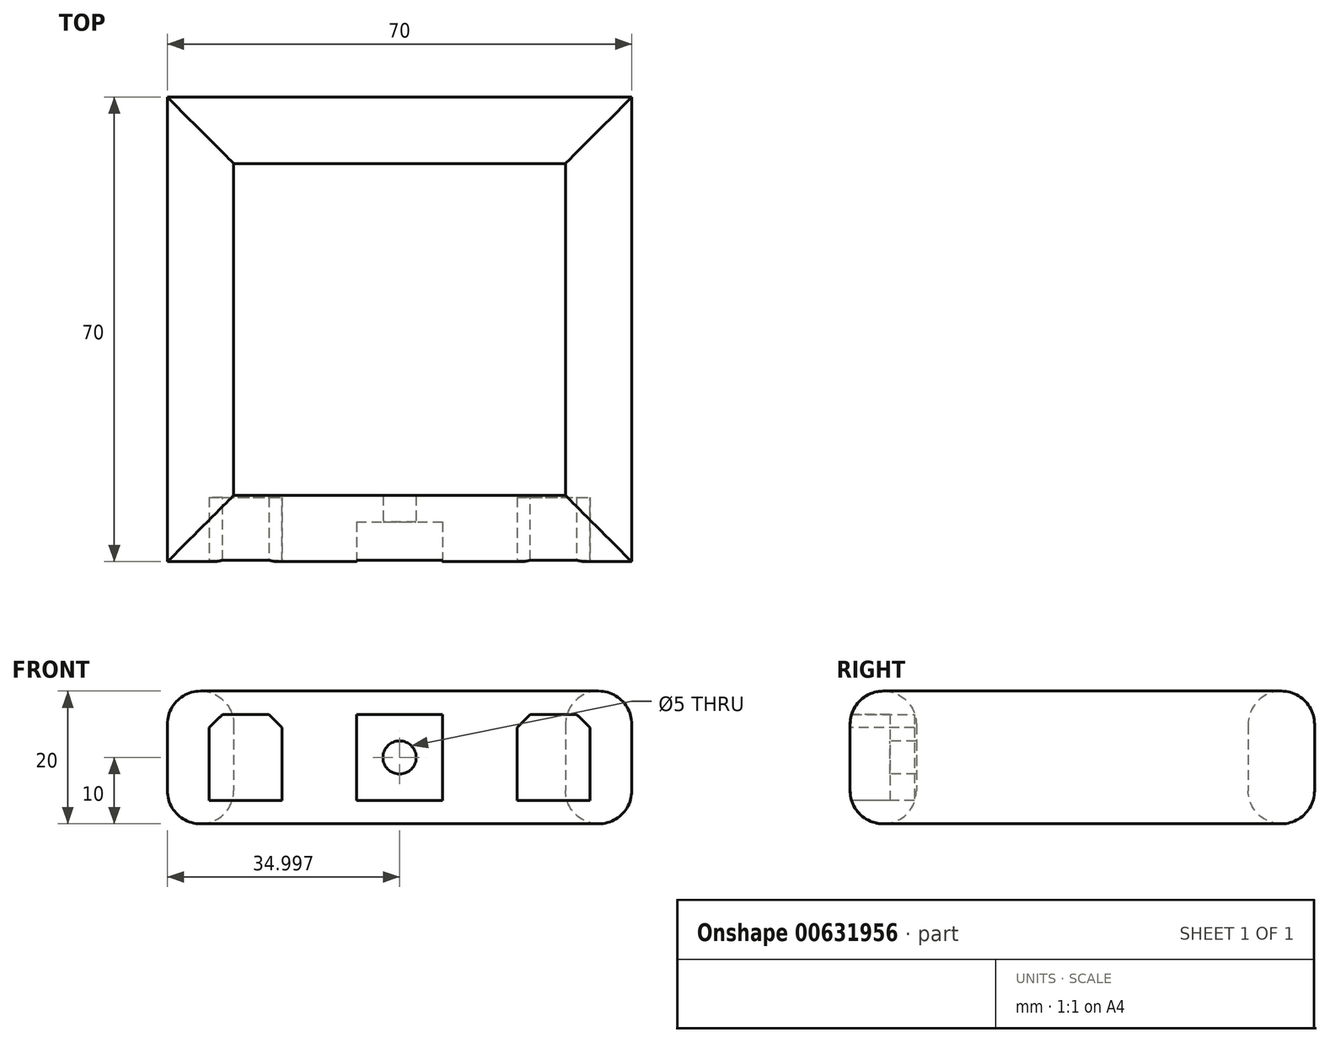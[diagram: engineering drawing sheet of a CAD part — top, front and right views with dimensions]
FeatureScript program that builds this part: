
annotation { "Feature Type Name" : "Feature", "Feature Type Description" : "" }
export const myFeature = defineFeature(function(context is Context, id is Id, definition is map)
    precondition{}
    {
        {
            var Q0;
            Q0=qCreatedBy(makeId("Top.planeOp"),FACE);
            var sketch = newSketch(context, id + "F0", { "sketchPlane" : qUnion([Q0])});
            skLineSegment(sketch, "E0.bottom", {"start": v(-28, 34.35) * mm, "end": v(42, 34.35) * mm});
            skLineSegment(sketch, "E0.top", {"start": v(-28, -35.65) * mm, "end": v(42, -35.65) * mm});
            skLineSegment(sketch, "E0.left", {"start": v(-28, 34.35) * mm, "end": v(-28, -35.65) * mm});
            skLineSegment(sketch, "E0.right", {"start": v(42, 34.35) * mm, "end": v(42, -35.65) * mm});
            skLineSegment(sketch, "E1.0", {"start": v(-18, 24.35) * mm, "end": v(-18, -25.65) * mm});
            skLineSegment(sketch, "E1.1", {"start": v(-18, 24.35) * mm, "end": v(32, 24.35) * mm});
            skLineSegment(sketch, "E1.2", {"start": v(32, 24.35) * mm, "end": v(32, -25.65) * mm});
            skLineSegment(sketch, "E1.3", {"start": v(-18, -25.65) * mm, "end": v(32, -25.65) * mm});
            skSolve(sketch);
        }
        {
            var Q0;
            Q0=makeQuery(id+"F0.imprint","IMPRINT",FACE,{"disambiguationData":[TD([[makeQuery(id+"F0.imprint","IMPRINT",EDGE,{"derivedFrom":sQuery(id+"F0.wireOp",EDGE,"E0.bottom")}),-1.0]])]});
            extrude(context, id + "F1", {"entities" : qUnion([Q0]), "depth" : 20 * mm, "offsetDistance" : 25 * mm});
        }
        {
            var Q0;
            Q0=makeQuery(id+"F1.opExtrude","SWEPT_FACE",FACE,{"disambiguationData":[OSD([sQuery(id+"F0.wireOp",EDGE,"E0.top")])]});
            var sketch = newSketch(context, id + "F2", { "sketchPlane" : qUnion([Q0])});
            skLineSegment(sketch, "E2.bottom", {"start": v(0.5, 16.5) * mm, "end": v(13.5, 16.5) * mm});
            skLineSegment(sketch, "E2.top", {"start": v(0.5, 3.5) * mm, "end": v(13.5, 3.5) * mm});
            skLineSegment(sketch, "E2.left", {"start": v(0.5, 16.5) * mm, "end": v(0.5, 3.5) * mm});
            skLineSegment(sketch, "E2.right", {"start": v(13.5, 16.5) * mm, "end": v(13.5, 3.5) * mm});
            skSolve(sketch);
        }
        {
            var Q0;
            Q0 = qSketchRegion(id + "F2", true);
            extrude(context, id + "F3", {"entities" : qUnion([Q0]), "operationType" : NewBodyOperationType.REMOVE, "oppositeDirection" : true, "depth" : 6 * mm, "offsetDistance" : 25 * mm});
        }
        {
            var Q0;
            Q0=makeQuery(id+"F7MwtvW5aFX19ho_1.boolean.opBoolean","MERGE",FACE,{"derivedFrom":[makeQuery(id+"FfgL2yHkp0veMAR_1.boolean.opBoolean","MERGE",FACE,{"derivedFrom":[makeQuery(id+"F1.opExtrude","CAP_FACE",FACE,{"disambiguationData":[OSD([sQuery(id+"F0.wireOp",EDGE,"E0.bottom"),sQuery(id+"F0.wireOp",EDGE,"E0.top"),sQuery(id+"F0.wireOp",EDGE,"E0.left"),sQuery(id+"F0.wireOp",EDGE,"E0.right"),sQuery(id+"F0.wireOp",EDGE,"E1.0"),sQuery(id+"F0.wireOp",EDGE,"E1.1"),sQuery(id+"F0.wireOp",EDGE,"E1.2"),sQuery(id+"F0.wireOp",EDGE,"E1.3")])],"isStart":false}),makeQuery(id+"FfgL2yHkp0veMAR_1.opExtrude","SWEPT_FACE",FACE,{"disambiguationData":[OSD([sQuery(id+"FrQLGLPTE21ChkL_1.wireOp",EDGE,"cfba748a-4d5a-4d7a-b181-aabee946887e.2")])]})]}),makeQuery(id+"F7MwtvW5aFX19ho_1.opExtrude","SWEPT_FACE",FACE,{"disambiguationData":[OSD([sQuery(id+"F9eCyIHyJgwxBDv_1.wireOp",EDGE,"g8lbYdjH-O4zc-bSOk-cj5n-4nt3Gmlz6ynf.top")])]})]});
            var Q1;
            Q1=makeQuery(id+"F7MwtvW5aFX19ho_1.boolean.opBoolean","MERGE",FACE,{"derivedFrom":[makeQuery(id+"FfgL2yHkp0veMAR_1.boolean.opBoolean","MERGE",FACE,{"derivedFrom":[makeQuery(id+"F1.opExtrude","CAP_FACE",FACE,{"disambiguationData":[OSD([sQuery(id+"F0.wireOp",EDGE,"E0.bottom"),sQuery(id+"F0.wireOp",EDGE,"E0.top"),sQuery(id+"F0.wireOp",EDGE,"E0.left"),sQuery(id+"F0.wireOp",EDGE,"E0.right"),sQuery(id+"F0.wireOp",EDGE,"E1.0"),sQuery(id+"F0.wireOp",EDGE,"E1.1"),sQuery(id+"F0.wireOp",EDGE,"E1.2"),sQuery(id+"F0.wireOp",EDGE,"E1.3")])],"isStart":true}),makeQuery(id+"FfgL2yHkp0veMAR_1.opExtrude","SWEPT_FACE",FACE,{"disambiguationData":[OSD([sQuery(id+"FrQLGLPTE21ChkL_1.wireOp",EDGE,"cfba748a-4d5a-4d7a-b181-aabee946887e.0")])]})]}),makeQuery(id+"F7MwtvW5aFX19ho_1.opExtrude","SWEPT_FACE",FACE,{"disambiguationData":[OSD([sQuery(id+"F9eCyIHyJgwxBDv_1.wireOp",EDGE,"g8lbYdjH-O4zc-bSOk-cj5n-4nt3Gmlz6ynf.bottom")])]})]});
            fillet(context, id + "F4", {"entities" : qUnion([Q0, Q1]), "radius" : 5 * mm, "tangentPropagation" : true, "allowEdgeOverflow" : false});
        }
        {
            var Q0;
            Q0=makeQuery(id+"F3.boolean.opBoolean","COPY",FACE,{"derivedFrom":makeQuery(id+"F3.opExtrude","CAP_FACE",FACE,{"disambiguationData":[OSD([sQuery(id+"F2.wireOp",EDGE,"E2.bottom"),sQuery(id+"F2.wireOp",EDGE,"E2.top"),sQuery(id+"F2.wireOp",EDGE,"E2.left"),sQuery(id+"F2.wireOp",EDGE,"E2.right")])],"isStart":false})});
            var sketch = newSketch(context, id + "F5", { "sketchPlane" : qUnion([Q0])});
            skCircle(sketch, "E3", {"center": v(7, 10) * mm, "radius": 2.5 * mm});
            skPoint(sketch, "E3.centerSnap0", {"position": v(7, 16.5) * mm});
            skPoint(sketch, "E3.centerSnap1", {"position": v(0.5, 10) * mm});
            skSolve(sketch);
        }
        {
            var Q0;
            Q0=makeQuery(id+"F5.imprint","IMPRINT",FACE,{"disambiguationData":[TD([[makeQuery(id+"F5.imprint","IMPRINT",EDGE,{"derivedFrom":sQuery(id+"F5.wireOp",EDGE,"E3")}),1.0]])]});
            extrude(context, id + "F6", {"entities" : qUnion([Q0]), "operationType" : NewBodyOperationType.REMOVE, "oppositeDirection" : true, "depth" : 25 * mm, "offsetDistance" : 25 * mm});
        }
        {
            var Q0;
            Q0=makeQuery(id+"F4.opFillet","SPLIT",FACE,{"disambiguationData":[OD(0.0)],"derivedFrom":makeQuery(id+"F1.opExtrude","SWEPT_FACE",FACE,{"disambiguationData":[OSD([sQuery(id+"F0.wireOp",EDGE,"E0.top")])]})});
            var sketch = newSketch(context, id + "F7", { "sketchPlane" : qUnion([Q0])});
            skLineSegment(sketch, "E4.bottom", {"start": v(-21.7, 16.5) * mm, "end": v(-10.7, 16.5) * mm});
            skLineSegment(sketch, "E4.top", {"start": v(-21.7, 3.5) * mm, "end": v(-10.7, 3.5) * mm});
            skLineSegment(sketch, "E4.left", {"start": v(-21.7, 16.5) * mm, "end": v(-21.7, 3.5) * mm});
            skLineSegment(sketch, "E4.right", {"start": v(-10.7, 16.5) * mm, "end": v(-10.7, 3.5) * mm});
            skLineSegment(sketch, "E5.1.0.0", {"start": v(24.7, 16.5) * mm, "end": v(24.7, 3.5) * mm});
            skLineSegment(sketch, "E5.1.0.1", {"start": v(24.7, 16.5) * mm, "end": v(35.7, 16.5) * mm});
            skLineSegment(sketch, "E5.1.0.2", {"start": v(35.7, 16.5) * mm, "end": v(35.7, 3.5) * mm});
            skLineSegment(sketch, "E5.1.0.3", {"start": v(24.7, 3.5) * mm, "end": v(35.7, 3.5) * mm});
            skLineSegment(sketch, "E5.direction1", {"start": v(-21.7, 3.5) * mm, "end": v(24.7, 3.5) * mm, "construction": true});
            skSolve(sketch);
        }
        {
            var Q0;
            {var subQ0=sQuery(id+"F7.wireOp",EDGE,"E4.left");var subQ1=sQuery(id+"F0.wireOp",EDGE,"E0.top");var subQ2=makeQuery(id+"F1.opExtrude","SWEPT_FACE",FACE,{"disambiguationData":[OSD([subQ1])]});var subQ3=makeQuery(id+"F4.opFillet","BLEND_EDGE",EDGE,{"disambiguationData":[OD(0.0)],"blendedFrom":[makeQuery(id+"F1.opExtrude","CAP_EDGE",EDGE,{"disambiguationData":[OSD([subQ1])],"isStart":false}),subQ2],"blendedInto":[subQ2]});var subQ4=makeQuery(id+"F7.imprint","INTERSECT",VERTEX,{"derivedFrom":[subQ3,subQ0]});Q0=makeQuery(id+"F7.imprint","IMPRINT",FACE,{"disambiguationData":[TD([[makeQuery(id+"F7.imprint","IMPRINT",EDGE,{"disambiguationData":[TD([[subQ4,-1.0]])],"derivedFrom":subQ0}),1.0]])]});}
            var Q1;
            {var subQ0=sQuery(id+"F7.wireOp",EDGE,"E4.bottom");Q1=makeQuery(id+"F7.imprint","IMPRINT",FACE,{"disambiguationData":[TD([[makeQuery(id+"F7.imprint","IMPRINT",EDGE,{"derivedFrom":subQ0}),-1.0]])]});}
            var Q2;
            {var subQ0=sQuery(id+"F7.wireOp",EDGE,"E4.top");Q2=makeQuery(id+"F7.imprint","IMPRINT",FACE,{"disambiguationData":[TD([[makeQuery(id+"F7.imprint","IMPRINT",EDGE,{"derivedFrom":subQ0}),1.0]])]});}
            var Q3;
            Q3=makeQuery(id+"F7.imprint","IMPRINT",FACE,{"disambiguationData":[TD([[makeQuery(id+"F7.imprint","IMPRINT",EDGE,{"derivedFrom":sQuery(id+"F7.wireOp",EDGE,"E5.1.0.0")}),1.0]])]});
            extrude(context, id + "F8", {"entities" : qUnion([Q0, Q1, Q2, Q3]), "operationType" : NewBodyOperationType.REMOVE, "oppositeDirection" : true, "depth" : 9.7 * mm, "offsetDistance" : 25 * mm});
        }
        {
            var Q0;
            Q0=makeQuery(id+"F8.boolean.opBoolean","COPY",EDGE,{"derivedFrom":makeQuery(id+"F8.opExtrude","SWEPT_EDGE",EDGE,{"disambiguationData":[OSD([sQuery(id+"F7.wireOp",EDGE,"E4.bottom"),sQuery(id+"F7.wireOp",EDGE,"E4.left")])]})});
            var Q1;
            Q1=makeQuery(id+"F8.boolean.opBoolean","COPY",EDGE,{"derivedFrom":makeQuery(id+"F8.opExtrude","SWEPT_EDGE",EDGE,{"disambiguationData":[OSD([sQuery(id+"F7.wireOp",EDGE,"E4.bottom"),sQuery(id+"F7.wireOp",EDGE,"E4.right")])]})});
            chamfer(context, id + "F9", {"entities" : qUnion([Q0, Q1]), "width" : 2 * mm, "tangentPropagation" : true});
        }
        {
            var Q0;
            Q0=makeQuery(id+"F8.boolean.opBoolean","COPY",EDGE,{"derivedFrom":makeQuery(id+"F8.opExtrude","SWEPT_EDGE",EDGE,{"disambiguationData":[OSD([sQuery(id+"F7.wireOp",EDGE,"E5.1.0.1"),sQuery(id+"F7.wireOp",EDGE,"E5.1.0.2")])]})});
            var Q1;
            Q1=makeQuery(id+"F8.boolean.opBoolean","COPY",EDGE,{"derivedFrom":makeQuery(id+"F8.opExtrude","SWEPT_EDGE",EDGE,{"disambiguationData":[OSD([sQuery(id+"F7.wireOp",EDGE,"E5.1.0.0"),sQuery(id+"F7.wireOp",EDGE,"E5.1.0.1")])]})});
            chamfer(context, id + "F10", {"entities" : qUnion([Q0, Q1]), "width" : 2 * mm, "tangentPropagation" : true});
        }
    });
